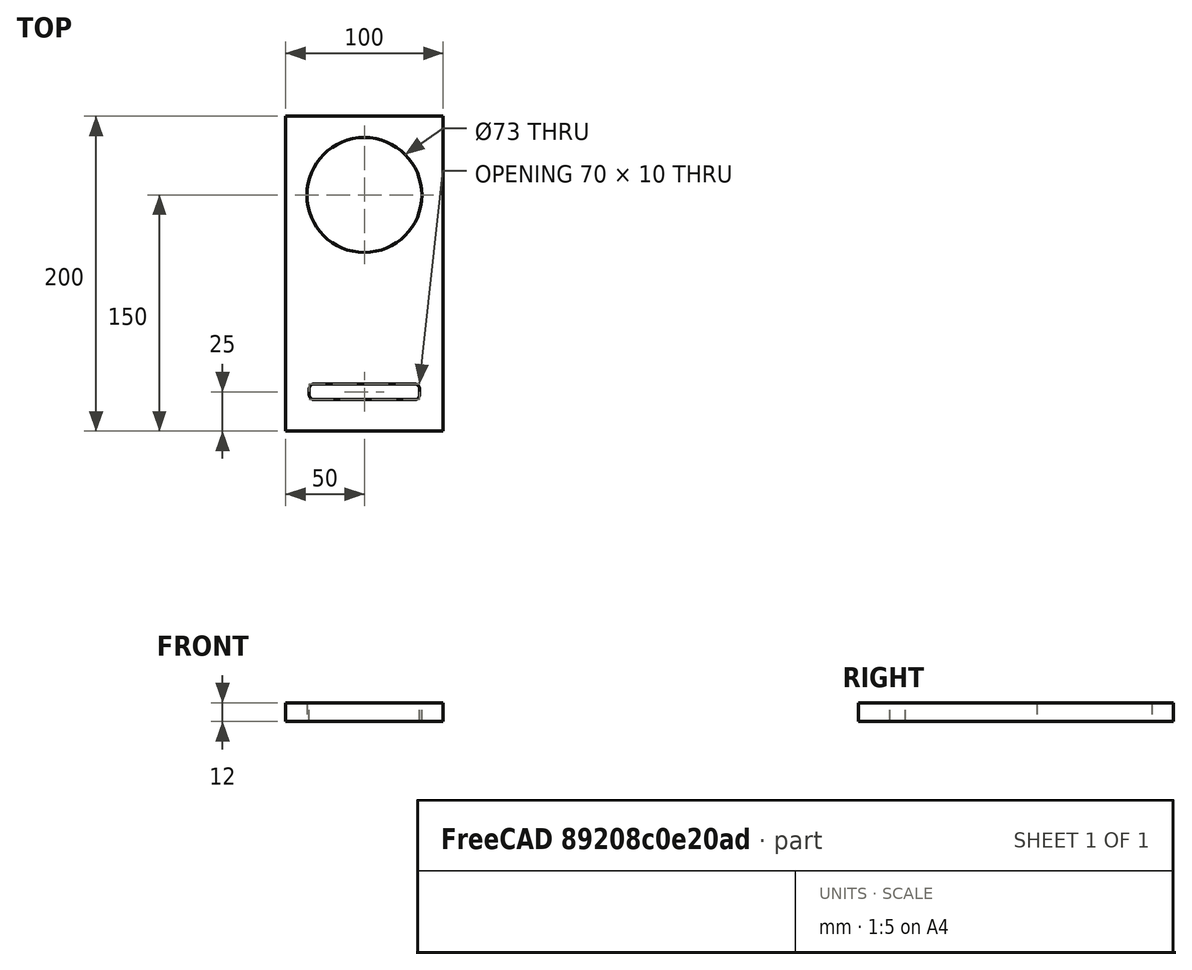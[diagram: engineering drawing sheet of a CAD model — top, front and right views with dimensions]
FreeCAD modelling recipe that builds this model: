
FCSTD DOCUMENT  (FreeCAD 0.16R6703 (Git))
Label: box2_front
License: All rights reserved
LicenseURL: http://en.wikipedia.org/wiki/All_rights_reserved
objects: Drawing::FeatureViewPython×10, Drawing::FeatureViewPart×2, Sketcher::SketchObject×1, PartDesign::Pad×1, Drawing::FeaturePage×1
note: 3 computed .brp shape members not serialized (recipe doc carries the construction recipe); baked Part::Feature solids carry a one-line shape summary decoded from their .brp

FEATURE [Sketcher::SketchObject] Sketch
  expr: Constraints[16] = 73 / 2
  sketch-geometry (14):
    g0: LineSegment StartX=0 StartY=0 StartZ=0 EndX=100 EndY=0 EndZ=0
    g1: LineSegment StartX=100 StartY=0 StartZ=0 EndX=100 EndY=200 EndZ=0
    g2: LineSegment StartX=100 StartY=200 StartZ=0 EndX=0 EndY=200 EndZ=0
    g3: LineSegment StartX=0 StartY=200 StartZ=0 EndX=0 EndY=0 EndZ=0
    g4: LineSegment [constr] StartX=0 StartY=150 StartZ=0 EndX=100 EndY=150 EndZ=0
    g5: Circle CenterX=50 CenterY=150 CenterZ=0 NormalX=0 NormalY=0 NormalZ=1 Radius=36.5
    g6: LineSegment StartX=18 StartY=20 StartZ=0 EndX=82 EndY=20 EndZ=0
    g7: LineSegment StartX=85 StartY=23 StartZ=0 EndX=85 EndY=27 EndZ=0
    g8: LineSegment StartX=82 StartY=30 StartZ=0 EndX=18 EndY=30 EndZ=0
    g9: LineSegment StartX=15 StartY=27 StartZ=0 EndX=15 EndY=23 EndZ=0
    g10: ArcOfCircle CenterX=18 CenterY=27 CenterZ=0 NormalX=0 NormalY=0 NormalZ=1 Radius=3 StartAngle=1.5708 EndAngle=3.14159
    g11: ArcOfCircle CenterX=18 CenterY=23 CenterZ=0 NormalX=0 NormalY=0 NormalZ=1 Radius=3 StartAngle=3.14159 EndAngle=4.71239
    g12: ArcOfCircle CenterX=82 CenterY=23 CenterZ=0 NormalX=0 NormalY=0 NormalZ=1 Radius=3 StartAngle=4.71239 EndAngle=6.28319
    g13: ArcOfCircle CenterX=82 CenterY=27 CenterZ=0 NormalX=0 NormalY=0 NormalZ=1 Radius=3 StartAngle=0 EndAngle=1.5708
  constraints (38):
    c: Coincident(g0,g1)
    c: Coincident(g1,g2)
    c: Coincident(g2,g3)
    c: Coincident(g3,g0)
    c: Horizontal(g0)
    c: Horizontal(g2)
    c: Vertical(g1)
    c: Vertical(g3)
    c: Coincident(g0,g-1)
    c: Distance(g1) = 200
    c: Distance(g0) = 100
    c: PointOnObject(g4,g3)
    c: PointOnObject(g4,g1)
    c: Horizontal(g4)
    c: PointOnObject(g5,g4)
    c: Symmetric(g4,g4,g5)
    c: Radius(g5) = 36.5
    c: DistanceY(g4,g2) = 50
    c: Horizontal(g6)
    c: Horizontal(g8)
    c: Vertical(g7)
    c: Vertical(g9)
    c: Tangent(g8,g10) = -1.5708
    c: Tangent(g9,g10) = -1.5708
    c: Tangent(g6,g11) = -1.5708
    c: Tangent(g9,g11) = -1.5708
    c: Tangent(g6,g12) = -1.5708
    c: Tangent(g7,g12) = -1.5708
    c: Tangent(g7,g13) = -1.5708
    c: Tangent(g8,g13) = -1.5708
    c: DistanceY(g6,g8) = 10
    c: DistanceX(g-1,g9) = 15
    c: DistanceX(g7,g0) = 15
    c: DistanceX(g11,g10) = 0
    c: DistanceX(g12,g13) = 0
    c: DistanceY(g-1,g6) = 20
    c: Equal(g10,g13)
    c: Radius(g13) = 3
FEATURE [PartDesign::Pad] Pad
  Length = 12
  Length2 = 100
  Sketch = -> Sketch
  Type = 0
FEATURE [Drawing::FeatureViewPart] Ortho  label="Ortho_0_0"
  Direction = (1,0,0)
  HiddenWidth = 0.15
  LineWidth = 0.35
  Rotation = -90
  Scale = 1.5
  ShowHiddenLines = false
  ShowSmoothLines = false
  Source = -> Pad
  Tolerance = 0.05
  ViewResult = <g id="Ortho_0_0"\n   transform="rotate(-90,60,44.3333) translate(60,44.3333) scale(1.5,1.5)"\n  >\n<g   stroke="rgb(0, 0, 0)"\n   stroke-width="0.233333"\n   stroke-linecap="butt"\n   stroke-linejoin="miter"\n   fill="none"\n   transform="scale(1,-1)"\n  >\n<path id= "1" d=" M 0 0 L 12 0 " />\n<path id= "2" d=" M 0 -200 L 12 -200 " />\n<path id= "3" d=" M 0 0 L 0 -200 " />\n<path id= "4" d=" M 12 0 L 12 -200 " />\n</g>\n</g>
  Visible = true
  X = 60
  Y = 44.3333
FEATURE [Drawing::FeatureViewPart] Ortho001  label="Ortho_0_-1"
  Direction = (0,0,-1)
  HiddenWidth = 0.15
  LineWidth = 0.35
  Rotation = 90
  Scale = 1.5
  ShowHiddenLines = false
  ShowSmoothLines = false
  Source = -> Pad
  Tolerance = 0.05
  ViewResult = <g id="Ortho_0_-1"\n   transform="rotate(90,60,210.667) translate(60,210.667) scale(1.5,1.5)"\n  >\n<g   stroke="rgb(0, 0, 0)"\n   stroke-width="0.233333"\n   stroke-linecap="butt"\n   stroke-linejoin="miter"\n   fill="none"\n   transform="scale(1,-1)"\n  >\n<path id= "1" d=" M 0 0 L -100 0 " />\n<path id= "2" d=" M -100 0 L -100 200 " />\n<path id= "3" d=" M -100 200 L 0 200 " />\n<path id= "4" d=" M 0 200 L 0 0 " />\n<circle cx ="-50" cy ="150" r ="36.5" /><path id= "6" d=" M -18 20 L -82 20 " />\n<path d="M-82 20 A3 3 0 0 0 -85 23" /><path id= "8" d=" M -85 23 L -85 27 " />\n<path d="M-85 27 A3 3 0 0 0 -82 30" /><path id= "10" d=" M -82 30 L -18 30 " />\n<path d="M-18 30 A3 3 0 0 0 -15 27" /><path id= "12" d=" M -15 27 L -15 23 " />\n<path d="M-15 23 A3 3 0 0 0 -18 20" /></g>\n</g>
  Visible = true
  X = 60
  Y = 210.667
FEATURE [Drawing::FeatureViewPython] dim002  # drawing view (typed FeaturePython)
  Rotation = 0
  ViewResult = <g> \n  <line x1="90.000000" y1="85.667000" x2="90.000000" y2="74.015162" style="stroke:rgb(0,0,255);stroke-width:0.50" />\n<line x1="105.000000" y1="85.667000" x2="105.000000" y2="74.015162" style="stroke:rgb(0,0,255);stroke-width:0.50" />\n<line x1="90.000000" y1="75.015162" x2="105.000000" y2="75.015162" style="stroke:rgb(0,0,255);stroke-width:0.50" /> \n  <polygon points="105.000000,75.015162 102.000000,74.015162 101.000000,75.015162 102.000000,76.015162" style="fill:rgb(0,0,255);stroke:rgb(0,0,255);stroke-width:0" /><polygon points="90.000000,75.015162 93.000000,76.015162 94.000000,75.015162 93.000000,74.015162" style="fill:rgb(0,0,255);stroke:rgb(0,0,255);stroke-width:0" /> \n  <text x="97.500000" y="73.015162" font-family="inherit" font-size="7" fill="rgb(0,0,255)" text-anchor="middle" transform="rotate(0.000000 97.500000,73.015162)" >10</text> </g>
  Visible = true
  X = 0
  Y = 0
  arrowL1 = 3
  arrowL2 = 1
  arrowW = 2
  arrow_scheme = 0
  autoPlaceOffset = 2
  autoPlaceText = true
  click1_x = 103.457
  click1_y = 75.0152
  click2_x = 103.457
  click2_y = 75.0152
  comma_decimal_place = false
  dimension_line_overshoot = 1
  gap_datum_points = 2
  halfDimension_linear = false
  lineColor = rgb(0,0,255)
  strokeWidth = 0.5
  textFormat_linear = %(value)3.3f
  textRenderer_color = rgb(0,0,255)
  textRenderer_family = inherit
  textRenderer_size = 7
  unit_custom_scale = 0.8
  unit_scheme = 0
FEATURE [Drawing::FeatureViewPython] dim004  # drawing view (typed FeaturePython)
  Rotation = 0
  ViewResult = <g> \n  <line x1="90.000000" y1="185.667000" x2="90.000000" y2="200.447895" style="stroke:rgb(0,0,255);stroke-width:0.50" />\n<line x1="60.000000" y1="208.667000" x2="60.000000" y2="198.447895" style="stroke:rgb(0,0,255);stroke-width:0.50" />\n<line x1="90.000000" y1="199.447895" x2="60.000000" y2="199.447895" style="stroke:rgb(0,0,255);stroke-width:0.50" /> \n  <polygon points="60.000000,199.447895 63.000000,200.447895 64.000000,199.447895 63.000000,198.447895" style="fill:rgb(0,0,255);stroke:rgb(0,0,255);stroke-width:0" /><polygon points="90.000000,199.447895 87.000000,198.447895 86.000000,199.447895 87.000000,200.447895" style="fill:rgb(0,0,255);stroke:rgb(0,0,255);stroke-width:0" /> \n  <text x="75.000000" y="197.447895" font-family="inherit" font-size="7" fill="rgb(0,0,255)" text-anchor="middle" transform="rotate(0.000000 75.000000,197.447895)" >20</text> </g>
  Visible = true
  X = 0
  Y = 0
  arrowL1 = 3
  arrowL2 = 1
  arrowW = 2
  arrow_scheme = 0
  autoPlaceOffset = 2
  autoPlaceText = true
  click1_x = 73.5931
  click1_y = 199.448
  click2_x = 73.5931
  click2_y = 199.448
  comma_decimal_place = false
  dimension_line_overshoot = 1
  gap_datum_points = 2
  halfDimension_linear = false
  lineColor = rgb(0,0,255)
  strokeWidth = 0.5
  textFormat_linear = %(value)3.3f
  textRenderer_color = rgb(0,0,255)
  textRenderer_family = inherit
  textRenderer_size = 7
  unit_custom_scale = 0.8
  unit_scheme = 0
FEATURE [Drawing::FeatureViewPython] dim005  # drawing view (typed FeaturePython)
  Rotation = 0
  ViewResult = <g> \n  <line x1="62.000000" y1="210.667000" x2="97.702010" y2="210.667000" style="stroke:rgb(0,0,255);stroke-width:0.50" />\n<line x1="96.500000" y1="188.167000" x2="97.702010" y2="188.167000" style="stroke:rgb(0,0,255);stroke-width:0.50" />\n<line x1="96.702010" y1="210.667000" x2="96.702010" y2="188.167000" style="stroke:rgb(0,0,255);stroke-width:0.50" /> \n  <polygon points="96.702010,188.167000 95.702010,191.167000 96.702010,192.167000 97.702010,191.167000" style="fill:rgb(0,0,255);stroke:rgb(0,0,255);stroke-width:0" /><polygon points="96.702010,210.667000 97.702010,207.667000 96.702010,206.667000 95.702010,207.667000" style="fill:rgb(0,0,255);stroke:rgb(0,0,255);stroke-width:0" /> \n  <text x="94.702010" y="199.417000" font-family="inherit" font-size="7" fill="rgb(0,0,255)" text-anchor="middle" transform="rotate(-90.000000 94.702010,199.417000)" >15</text> </g>
  Visible = true
  X = 0
  Y = 0
  arrowL1 = 3
  arrowL2 = 1
  arrowW = 2
  arrow_scheme = 0
  autoPlaceOffset = 2
  autoPlaceText = true
  click1_x = 96.702
  click1_y = 195.893
  click2_x = 96.702
  click2_y = 195.893
  comma_decimal_place = false
  dimension_line_overshoot = 1
  gap_datum_points = 2
  halfDimension_linear = false
  lineColor = rgb(0,0,255)
  strokeWidth = 0.5
  textFormat_linear = %(value)3.3f
  textRenderer_color = rgb(0,0,255)
  textRenderer_family = inherit
  textRenderer_size = 7
  unit_custom_scale = 0.8
  unit_scheme = 0
FEATURE [Drawing::FeatureViewPython] dim006  # drawing view (typed FeaturePython)
  Rotation = 0
  ViewResult = <g> \n  <line x1="102.500000" y1="188.167000" x2="125.077211" y2="188.167000" style="stroke:rgb(0,0,255);stroke-width:0.50" />\n<line x1="102.500000" y1="83.167000" x2="125.077211" y2="83.167000" style="stroke:rgb(0,0,255);stroke-width:0.50" />\n<line x1="124.077211" y1="188.167000" x2="124.077211" y2="83.167000" style="stroke:rgb(0,0,255);stroke-width:0.50" /> \n  <polygon points="124.077211,83.167000 123.077211,86.167000 124.077211,87.167000 125.077211,86.167000" style="fill:rgb(0,0,255);stroke:rgb(0,0,255);stroke-width:0" /><polygon points="124.077211,188.167000 125.077211,185.167000 124.077211,184.167000 123.077211,185.167000" style="fill:rgb(0,0,255);stroke:rgb(0,0,255);stroke-width:0" /> \n  <text x="122.077211" y="135.667000" font-family="inherit" font-size="7" fill="rgb(0,0,255)" text-anchor="middle" transform="rotate(-90.000000 122.077211,135.667000)" >70</text> </g>
  Visible = true
  X = 0
  Y = 0
  arrowL1 = 3
  arrowL2 = 1
  arrowW = 2
  arrow_scheme = 0
  autoPlaceOffset = 2
  autoPlaceText = true
  click1_x = 124.077
  click1_y = 81.7701
  click2_x = 124.077
  click2_y = 81.7701
  comma_decimal_place = false
  dimension_line_overshoot = 1
  gap_datum_points = 2
  halfDimension_linear = false
  lineColor = rgb(0,0,255)
  strokeWidth = 0.5
  textFormat_linear = %(value)3.3f
  textRenderer_color = rgb(0,0,255)
  textRenderer_family = inherit
  textRenderer_size = 7
  unit_custom_scale = 0.8
  unit_scheme = 0
FEATURE [Drawing::FeatureViewPython] dim007  # drawing view (typed FeaturePython)
  Rotation = 0
  ViewResult = <g> \n  <line x1="283.000000" y1="80.917000" x2="204.136249" y2="80.917000" style="stroke:rgb(0,0,255);stroke-width:0.50" />\n<line x1="283.000000" y1="190.417000" x2="204.136249" y2="190.417000" style="stroke:rgb(0,0,255);stroke-width:0.50" />\n<line x1="205.136249" y1="80.917000" x2="205.136249" y2="190.417000" style="stroke:rgb(0,0,255);stroke-width:0.50" /> \n  <polygon points="205.136249,190.417000 206.136249,187.417000 205.136249,186.417000 204.136249,187.417000" style="fill:rgb(0,0,255);stroke:rgb(0,0,255);stroke-width:0" /><polygon points="205.136249,80.917000 204.136249,83.917000 205.136249,84.917000 206.136249,83.917000" style="fill:rgb(0,0,255);stroke:rgb(0,0,255);stroke-width:0" /> \n  <text x="203.136249" y="135.667000" font-family="inherit" font-size="7" fill="rgb(0,0,255)" text-anchor="middle" transform="rotate(-90.000000 203.136249,135.667000)" >73</text> </g>
  Visible = true
  X = 0
  Y = 0
  arrowL1 = 3
  arrowL2 = 1
  arrowW = 2
  arrow_scheme = 0
  autoPlaceOffset = 2
  autoPlaceText = true
  click1_x = 205.136
  click1_y = 188.071
  click2_x = 205.136
  click2_y = 188.071
  comma_decimal_place = false
  dimension_line_overshoot = 1
  gap_datum_points = 2
  halfDimension_linear = false
  lineColor = rgb(0,0,255)
  strokeWidth = 0.5
  textFormat_linear = %(value)3.3f
  textRenderer_color = rgb(0,0,255)
  textRenderer_family = inherit
  textRenderer_size = 7
  unit_custom_scale = 0.8
  unit_scheme = 0
FEATURE [Drawing::FeatureViewPython] dim008  # drawing view (typed FeaturePython)
  Rotation = 0
  ViewResult = <g> \n  <line x1="285.000000" y1="133.667000" x2="285.000000" y2="118.099902" style="stroke:rgb(0,0,255);stroke-width:0.50" />\n<line x1="360.000000" y1="208.667000" x2="360.000000" y2="118.099902" style="stroke:rgb(0,0,255);stroke-width:0.50" />\n<line x1="285.000000" y1="119.099902" x2="360.000000" y2="119.099902" style="stroke:rgb(0,0,255);stroke-width:0.50" /> \n  <polygon points="360.000000,119.099902 357.000000,118.099902 356.000000,119.099902 357.000000,120.099902" style="fill:rgb(0,0,255);stroke:rgb(0,0,255);stroke-width:0" /><polygon points="285.000000,119.099902 288.000000,120.099902 289.000000,119.099902 288.000000,118.099902" style="fill:rgb(0,0,255);stroke:rgb(0,0,255);stroke-width:0" /> \n  <text x="322.500000" y="117.099902" font-family="inherit" font-size="7" fill="rgb(0,0,255)" text-anchor="middle" transform="rotate(0.000000 322.500000,117.099902)" >50</text> </g>
  Visible = true
  X = 0
  Y = 0
  arrowL1 = 3
  arrowL2 = 1
  arrowW = 2
  arrow_scheme = 0
  autoPlaceOffset = 2
  autoPlaceText = true
  click1_x = 316.77
  click1_y = 119.1
  click2_x = 316.77
  click2_y = 119.1
  comma_decimal_place = false
  dimension_line_overshoot = 1
  gap_datum_points = 2
  halfDimension_linear = false
  lineColor = rgb(0,0,255)
  strokeWidth = 0.5
  textFormat_linear = %(value)3.3f
  textRenderer_color = rgb(0,0,255)
  textRenderer_family = inherit
  textRenderer_size = 7
  unit_custom_scale = 0.8
  unit_scheme = 0
FEATURE [Drawing::FeatureViewPython] dim009  # drawing view (typed FeaturePython)
  Rotation = 0
  ViewResult = <g> \n  <line x1="283.000000" y1="135.667000" x2="274.529623" y2="135.667000" style="stroke:rgb(0,0,255);stroke-width:0.50" />\n<line x1="358.000000" y1="210.667000" x2="274.529623" y2="210.667000" style="stroke:rgb(0,0,255);stroke-width:0.50" />\n<line x1="275.529623" y1="135.667000" x2="275.529623" y2="210.667000" style="stroke:rgb(0,0,255);stroke-width:0.50" /> \n  <polygon points="275.529623,210.667000 276.529623,207.667000 275.529623,206.667000 274.529623,207.667000" style="fill:rgb(0,0,255);stroke:rgb(0,0,255);stroke-width:0" /><polygon points="275.529623,135.667000 274.529623,138.667000 275.529623,139.667000 276.529623,138.667000" style="fill:rgb(0,0,255);stroke:rgb(0,0,255);stroke-width:0" /> \n  <text x="273.529623" y="173.167000" font-family="inherit" font-size="7" fill="rgb(0,0,255)" text-anchor="middle" transform="rotate(-90.000000 273.529623,173.167000)" >50</text> </g>
  Visible = true
  X = 0
  Y = 0
  arrowL1 = 3
  arrowL2 = 1
  arrowW = 2
  arrow_scheme = 0
  autoPlaceOffset = 2
  autoPlaceText = true
  click1_x = 275.53
  click1_y = 200.87
  click2_x = 275.53
  click2_y = 200.87
  comma_decimal_place = false
  dimension_line_overshoot = 1
  gap_datum_points = 2
  halfDimension_linear = false
  lineColor = rgb(0,0,255)
  strokeWidth = 0.5
  textFormat_linear = %(value)3.3f
  textRenderer_color = rgb(0,0,255)
  textRenderer_family = inherit
  textRenderer_size = 7
  unit_custom_scale = 0.8
  unit_scheme = 0
FEATURE [Drawing::FeatureViewPython] dim010  # drawing view (typed FeaturePython)
  Rotation = 0
  ViewResult = <g> \n  <line x1="58.000000" y1="44.333300" x2="44.862350" y2="44.333300" style="stroke:rgb(0,0,255);stroke-width:0.50" />\n<line x1="58.000000" y1="26.333300" x2="44.862350" y2="26.333300" style="stroke:rgb(0,0,255);stroke-width:0.50" />\n<line x1="45.862350" y1="44.333300" x2="45.862350" y2="26.333300" style="stroke:rgb(0,0,255);stroke-width:0.50" /> \n  <polygon points="45.862350,26.333300 44.862350,29.333300 45.862350,30.333300 46.862350,29.333300" style="fill:rgb(0,0,255);stroke:rgb(0,0,255);stroke-width:0" /><polygon points="45.862350,44.333300 46.862350,41.333300 45.862350,40.333300 44.862350,41.333300" style="fill:rgb(0,0,255);stroke:rgb(0,0,255);stroke-width:0" /> \n  <text x="43.862350" y="35.333300" font-family="inherit" font-size="7" fill="rgb(0,0,255)" text-anchor="middle" transform="rotate(-90.000000 43.862350,35.333300)" >12</text> </g>
  Visible = true
  X = 0
  Y = 0
  arrowL1 = 3
  arrowL2 = 1
  arrowW = 2
  arrow_scheme = 0
  autoPlaceOffset = 2
  autoPlaceText = true
  click1_x = 45.8624
  click1_y = 32.3525
  click2_x = 45.8624
  click2_y = 32.3525
  comma_decimal_place = false
  dimension_line_overshoot = 1
  gap_datum_points = 2
  halfDimension_linear = false
  lineColor = rgb(0,0,255)
  strokeWidth = 0.5
  textFormat_linear = %(value)3.3f
  textRenderer_color = rgb(0,0,255)
  textRenderer_family = inherit
  textRenderer_size = 7
  unit_custom_scale = 0.8
  unit_scheme = 0
FEATURE [Drawing::FeatureViewPython] dim011  # drawing view (typed FeaturePython)
  Rotation = 0
  ViewResult = <g> \n  <line x1="58.000000" y1="210.667000" x2="45.928916" y2="210.667000" style="stroke:rgb(0,0,255);stroke-width:0.50" />\n<line x1="58.000000" y1="60.667000" x2="45.928916" y2="60.667000" style="stroke:rgb(0,0,255);stroke-width:0.50" />\n<line x1="46.928916" y1="210.667000" x2="46.928916" y2="60.667000" style="stroke:rgb(0,0,255);stroke-width:0.50" /> \n  <polygon points="46.928916,60.667000 45.928916,63.667000 46.928916,64.667000 47.928916,63.667000" style="fill:rgb(0,0,255);stroke:rgb(0,0,255);stroke-width:0" /><polygon points="46.928916,210.667000 47.928916,207.667000 46.928916,206.667000 45.928916,207.667000" style="fill:rgb(0,0,255);stroke:rgb(0,0,255);stroke-width:0" /> \n  <text x="44.928916" y="135.667000" font-family="inherit" font-size="7" fill="rgb(0,0,255)" text-anchor="middle" transform="rotate(-90.000000 44.928916,135.667000)" >100</text> </g>
  Visible = true
  X = 0
  Y = 0
  arrowL1 = 3
  arrowL2 = 1
  arrowW = 2
  arrow_scheme = 0
  autoPlaceOffset = 2
  autoPlaceText = true
  click1_x = 46.9289
  click1_y = 80.7035
  click2_x = 46.9289
  click2_y = 80.7035
  comma_decimal_place = false
  dimension_line_overshoot = 1
  gap_datum_points = 2
  halfDimension_linear = false
  lineColor = rgb(0,0,255)
  strokeWidth = 0.5
  textFormat_linear = %(value)3.3f
  textRenderer_color = rgb(0,0,255)
  textRenderer_family = inherit
  textRenderer_size = 7
  unit_custom_scale = 0.8
  unit_scheme = 0
FEATURE [Drawing::FeatureViewPython] dim012  # drawing view (typed FeaturePython)
  Rotation = 0
  ViewResult = <g> \n  <line x1="360.000000" y1="212.667000" x2="360.000000" y2="224.623398" style="stroke:rgb(0,0,255);stroke-width:0.50" />\n<line x1="60.000000" y1="212.667000" x2="60.000000" y2="224.623398" style="stroke:rgb(0,0,255);stroke-width:0.50" />\n<line x1="360.000000" y1="223.623398" x2="60.000000" y2="223.623398" style="stroke:rgb(0,0,255);stroke-width:0.50" /> \n  <polygon points="60.000000,223.623398 63.000000,224.623398 64.000000,223.623398 63.000000,222.623398" style="fill:rgb(0,0,255);stroke:rgb(0,0,255);stroke-width:0" /><polygon points="360.000000,223.623398 357.000000,222.623398 356.000000,223.623398 357.000000,224.623398" style="fill:rgb(0,0,255);stroke:rgb(0,0,255);stroke-width:0" /> \n  <text x="210.000000" y="221.623398" font-family="inherit" font-size="7" fill="rgb(0,0,255)" text-anchor="middle" transform="rotate(0.000000 210.000000,221.623398)" >200</text> </g>
  Visible = true
  X = 0
  Y = 0
  arrowL1 = 3
  arrowL2 = 1
  arrowW = 2
  arrow_scheme = 0
  autoPlaceOffset = 2
  autoPlaceText = true
  click1_x = 161.763
  click1_y = 223.623
  click2_x = 161.763
  click2_y = 223.623
  comma_decimal_place = false
  dimension_line_overshoot = 1
  gap_datum_points = 2
  halfDimension_linear = false
  lineColor = rgb(0,0,255)
  strokeWidth = 0.5
  textFormat_linear = %(value)3.3f
  textRenderer_color = rgb(0,0,255)
  textRenderer_family = inherit
  textRenderer_size = 7
  unit_custom_scale = 0.8
  unit_scheme = 0
FEATURE [Drawing::FeaturePage] Page
  EditableTexts = AUTHOR NAME | CREATION DATE | SUPERVISOR NAME | CHECK DATE | SCALE | WEIGHT | NUMBER | SHEET | box 2 front | SUBTITLE
  Group = -> [Ortho,Ortho001,dim002,dim004,dim005,dim006,dim007,dim008,dim009,dim010,dim011,dim012]
